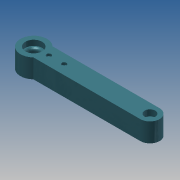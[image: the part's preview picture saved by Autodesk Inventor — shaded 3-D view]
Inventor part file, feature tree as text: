
AUTODESK INVENTOR PART (.ipt)
format: ipt  version: 2013 (Build 170138000, 138)  size: 133,632 bytes
history: native  units: mm
features: extrude x6, sketch x6, fillet x1
ambient origin geometry x8: Origin, YZ Plane, XZ Plane, XY Plane, X Axis, Y Axis, Z Axis, Center Point
bodies: Solid1 (feature_tree)
feature tree (13):
  extrude  "Extrusion1"  Depth=12.6mm
  extrude  "Extrusion2"  Depth=8.5mm
  extrude  "Extrusion3"  Depth=22.0mm
  extrude  "Extrusion4"  Depth=20.0mm
  extrude  "Extrusion5"  Depth=7.0mm TaperAngle=0.0deg
  extrude  "Extrusion6"  Depth=3.5mm
  fillet  "Fillet1"  Radius=35.0mm
  sketch  "Sketch1"  dims[d0=153.0mm d2=12.6mm]
  sketch  "Sketch2"  dims[d3=15.0mm d4=8.5mm]
  sketch  "Sketch4"  dims[d5=25.0mm d6=0.0mm d7=22.0mm]
  sketch  "Sketch5"  dims[d9=7.0mm d10=0.0mm d16=20.0mm]
  sketch  "Sketch6"  dims[d17=40.0mm d18=7.0mm d19=0.0mm]
  sketch  "Sketch7"  dims[d21=3.0mm d22=0.0mm d23=3.5mm d24=35.0mm d26=10.0mm d27=0.0mm d28=6.0mm d30=14.0mm d32=8.0mm d33=0.0mm d34=3.5mm]
